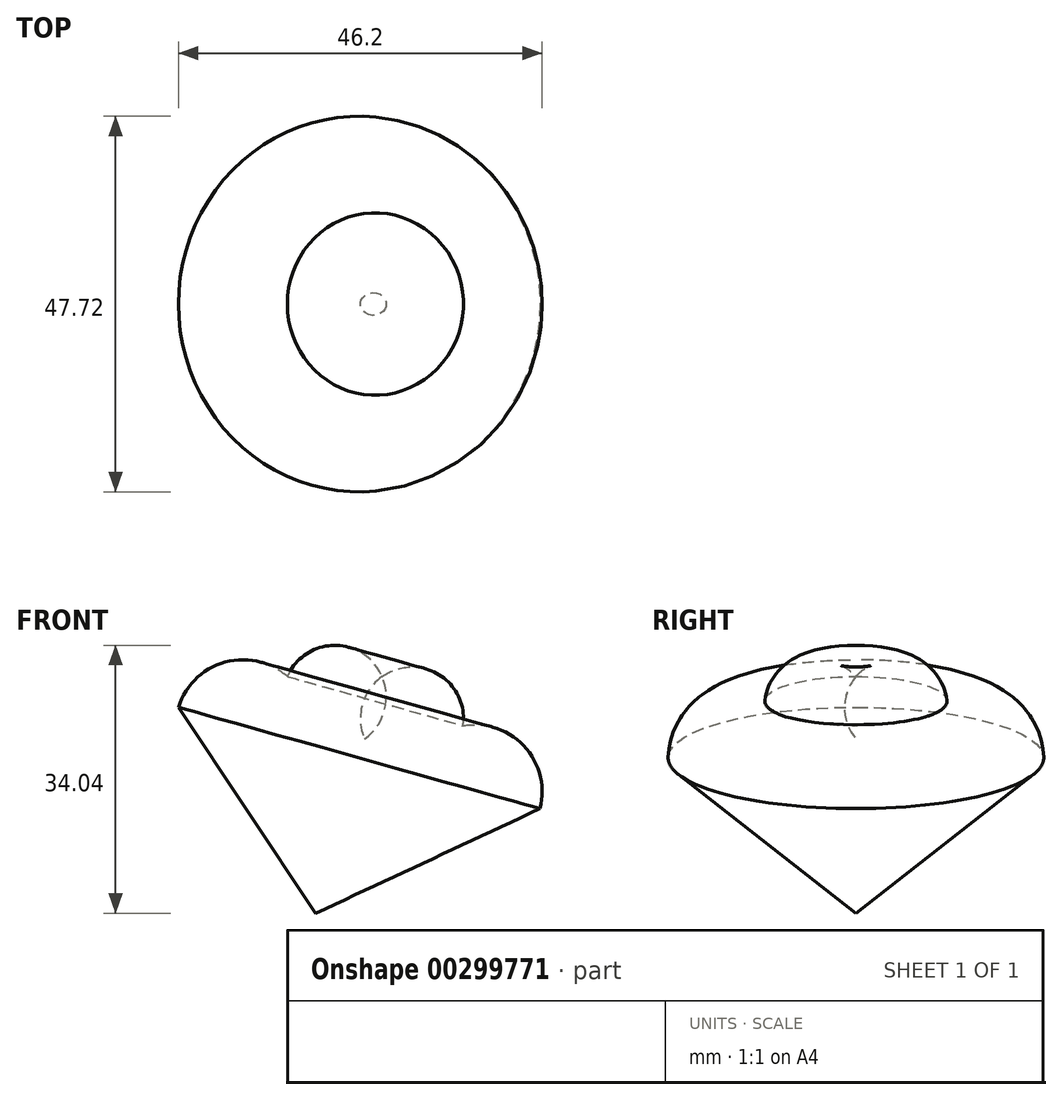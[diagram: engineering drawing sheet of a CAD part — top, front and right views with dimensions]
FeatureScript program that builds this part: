
annotation { "Feature Type Name" : "Feature", "Feature Type Description" : "" }
export const myFeature = defineFeature(function(context is Context, id is Id, definition is map)
    precondition{}
    {
        {
            var Q0;
            Q0=qCreatedBy(makeId("Front.planeOp"),FACE);
            var sketch = newSketch(context, id + "F0", { "sketchPlane" : qUnion([Q0])});
            skArc(sketch, "E0", {"start": v(-40.6, 56.55) * mm, "mid": v(-48.59, 58.36) * mm, "end": v(-54.44, 52.64) * mm});
            skArc(sketch, "E1", {"start": v(-28.57, 56.55) * mm, "mid": v(-34.6, 60.51) * mm, "end": v(-40.6, 56.55) * mm});
            skLineSegment(sketch, "E2", {"start": v(-54.44, 52.64) * mm, "end": v(-37, 26.47) * mm});
            skLineSegment(sketch, "E3", {"start": v(-37, 26.47) * mm, "end": v(-28.57, 56.55) * mm});
            skSolve(sketch);
        }
        {
            var Q0;
            Q0=makeQuery(id+"F0.imprint","IMPRINT",FACE,{"disambiguationData":[TD([[makeQuery(id+"F0.imprint","IMPRINT",EDGE,{"derivedFrom":sQuery(id+"F0.wireOp",EDGE,"E0")}),1.0]])]});
            var Q1;
            Q1=sQuery(id+"F0.wireOp",EDGE,"E3");
            revolve(context, id + "F1", {"entities" : qUnion([Q0]), "axis" : qUnion([Q1]), "revolveType" : RevolveType.FULL});
        }
    });
